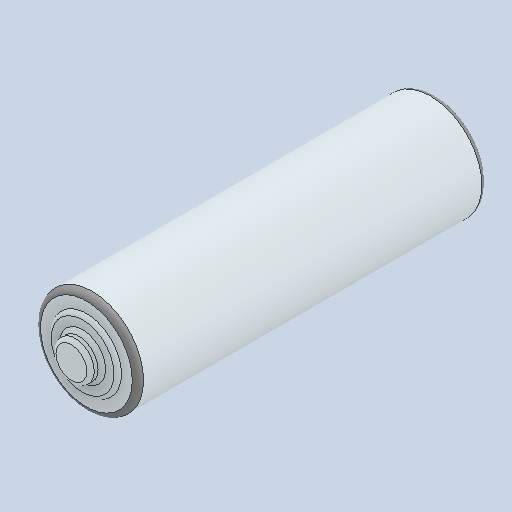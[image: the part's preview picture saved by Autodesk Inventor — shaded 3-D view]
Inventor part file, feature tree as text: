
AUTODESK INVENTOR PART (.ipt)
format: ipt  version: 2024 (Build 280153000, 153)  size: 125,952 bytes
history: native  units: in
note: dims shown in document units (in); Inventor stores cm internally (conversion verified against a paired STEP export)
features: other x1, fillet x1
ambient origin geometry x8: Origin, YZ Plane, XZ Plane, XY Plane, X Axis, Y Axis, Z Axis, Center Point
bodies: Solid1 (feature_tree)
feature tree (2):
  other  "Assi1"
  fillet  "Fillet9"  [1 undecoded]
note: 1 required parameter value undecoded (feature->parameter linkage not recoverable at this tier; creation-order binding heuristic only, values carry confidence <= 0.55)
